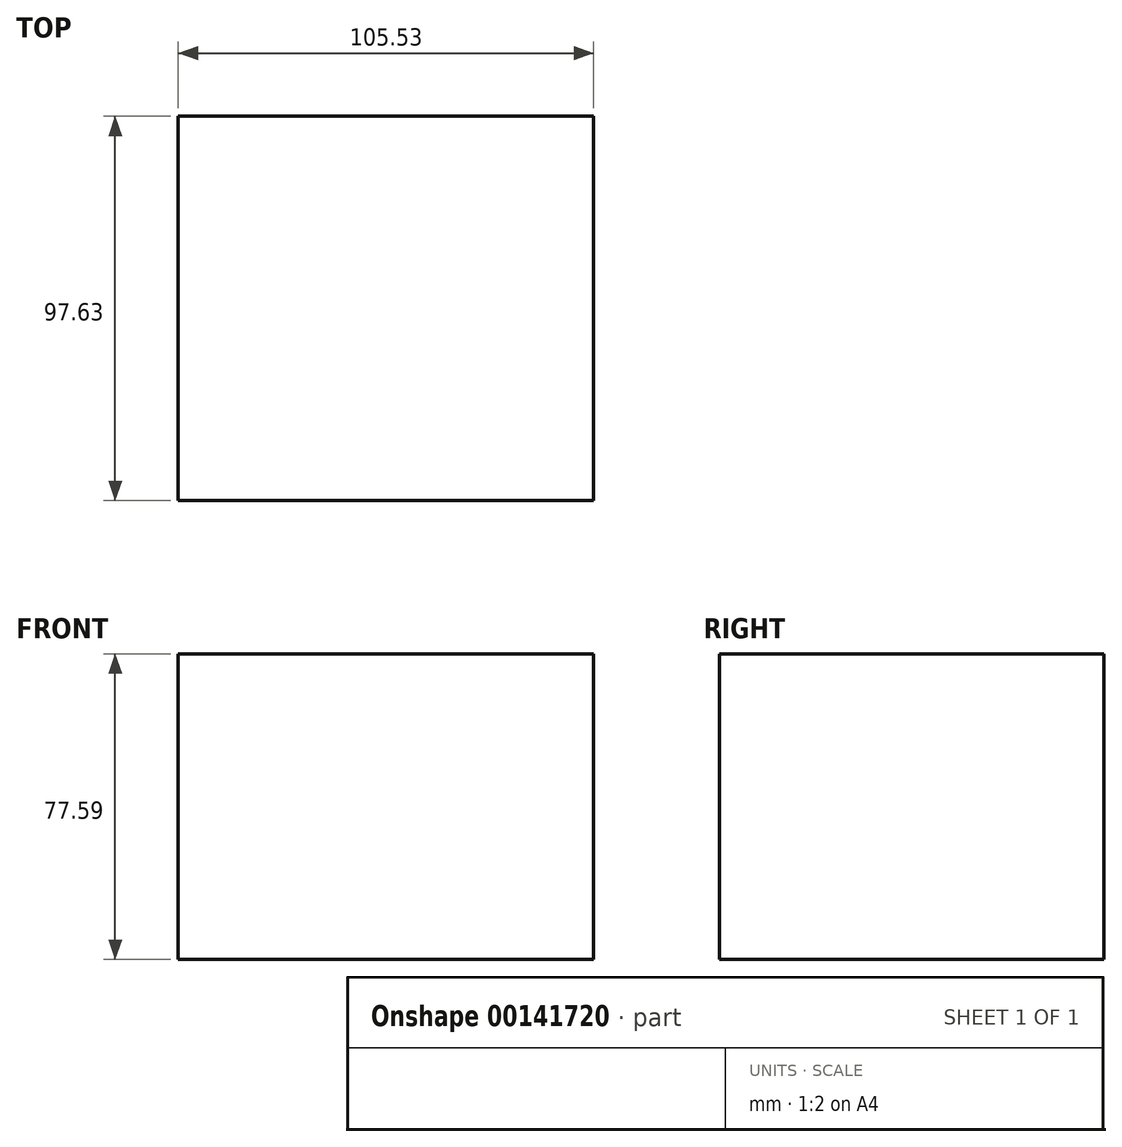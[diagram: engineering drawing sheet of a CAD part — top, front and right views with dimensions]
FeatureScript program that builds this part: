
annotation { "Feature Type Name" : "Feature", "Feature Type Description" : "" }
export const myFeature = defineFeature(function(context is Context, id is Id, definition is map)
    precondition{}
    {
        {
            var Q0;
            Q0=qCreatedBy(makeId("Front.planeOp"),FACE);
            var sketch = newSketch(context, id + "F0", { "sketchPlane" : qUnion([Q0])});
            skLineSegment(sketch, "E0.bottom", {"start": v(-147.88, 77.6) * mm, "end": v(-42.35, 77.6) * mm});
            skLineSegment(sketch, "E0.top", {"start": v(-147.88, 0) * mm, "end": v(-42.35, 0) * mm});
            skLineSegment(sketch, "E0.left", {"start": v(-147.88, 77.6) * mm, "end": v(-147.88, 0) * mm});
            skLineSegment(sketch, "E0.right", {"start": v(-42.35, 77.6) * mm, "end": v(-42.35, 0) * mm});
            skSolve(sketch);
        }
        {
            var Q0;
            Q0=makeQuery(id+"F0.imprint","IMPRINT",FACE,{"disambiguationData":[TD([[makeQuery(id+"F0.imprint","IMPRINT",EDGE,{"derivedFrom":sQuery(id+"F0.wireOp",EDGE,"E0.bottom")}),-1.0]])]});
            extrude(context, id + "F1", {"entities" : qUnion([Q0]), "depth" : 97.63 * mm});
        }
    });
